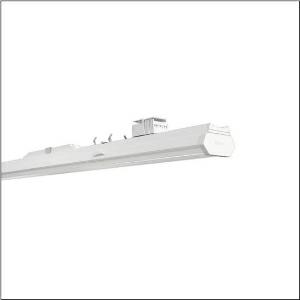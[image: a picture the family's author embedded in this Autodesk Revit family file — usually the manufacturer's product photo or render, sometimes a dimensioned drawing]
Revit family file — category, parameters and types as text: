
# Revit family: licross_r__11_protected_mo_51tp12dn49xf3c_1f2d
name_source: partatom
category: Lighting Fixtures
units: mm (PartAtom-declared; Revit-internal decimal feet)

## family parameters
Cut with Voids When Loaded = No
Host = Face
Light Source = No
Part Type = Normal
Room Calculation Point = No
Round Connector Dimension = Use Diameter
Shared = No

## types (1)
- --- (1 x LED, 870 lm, 5 W, 4000K)
    Apparent Load = 5 VA
    CIE Flux Codes = 73 92 98 99 100
    Color Rendering = 80
    Color Temperature = 4000K
    Default Elevation = 1800 mm
    Description = Licross® 11 Protected MO, luminaire insert, of sheet steel, galvanised, coil coated, white, length: 1.500mm, width: 90mm, height: 101mm, LED rated luminous flux: 9.020lm, light colour: 840, control gear: DALI 2, control gear: ECG DALI, with plug, 6-pole, with phase selection, for trunking rail, 14-core, mains connection: 220..240V, AC/DC, 0/50..60Hz, halogen-free wiring, for emergency light function, charging phase on R (wire number 6), converter,control gear: single battery element, battery: LiFeP04, 9Ah, primary optical cover: cover, of PMMA, light emission: direct with ceiling illumination distribution, protection rating (complete): IP64, insulation class (complete): insulation class I (protective earthing), certification: CE, UKCA, protection symbol: D if used in an environment with conductive dust loads with corresponding accessories, permissible ambient temperature for indoor applications: +5..+35°C, standard: EN 60598-2-22, corresponds to IFS (International Featured Standards) requirements for safety and quality in the food industry, reducing of maximum allowable ambient temperature of 5°C with ceiling mounting, LABS conformity tested according to VDMA 24364:2018-05, packaging unit: 1 piece
    Height = 92 mm
    Lamp = 1 x LED
    Lamp Light Flux = 870 lm
    Lamp Power = 5 W
    Lamp count = 1
    Length = 1500 mm
    Luminous efficacy = 174 lm/W
    Manufacturer = Siteco
    ModVariant = No
    Model = 51TP12DN49XF3C
    Mounting Place = Ceiling
    Mounting Type = Pendant
    Number of Poles = 1
    OnlyDefault = Yes
    Power Factor = 1
    Product Name = Licross® 11 Protected MO
    Product group = luminaire insert
    ProductGroupID = 902
    Protection Class = Protection class I
    Protection Degree = IP 64
    RLX_Detail_Level = 1
    RlxData = <blob elided: 24781 chars, md5=9082d4c5>
    Socket = socket
    Standby Power = 0 W
    System Light Flux = 870 lm
    System Power = 5 W
    Type Comments = : emergency light operation: 3 h
    Type Image = l_1256148.jpg
    URL = http://relux.com
    VarID = @adj_126037
    Voltage = 0 V
    Weight = 0.00 kg
    Width = 88 mm

## geometry (parser evidence)
native form markers: Blend x4, Sweep x9
no freeform markers — native parametric forms only
